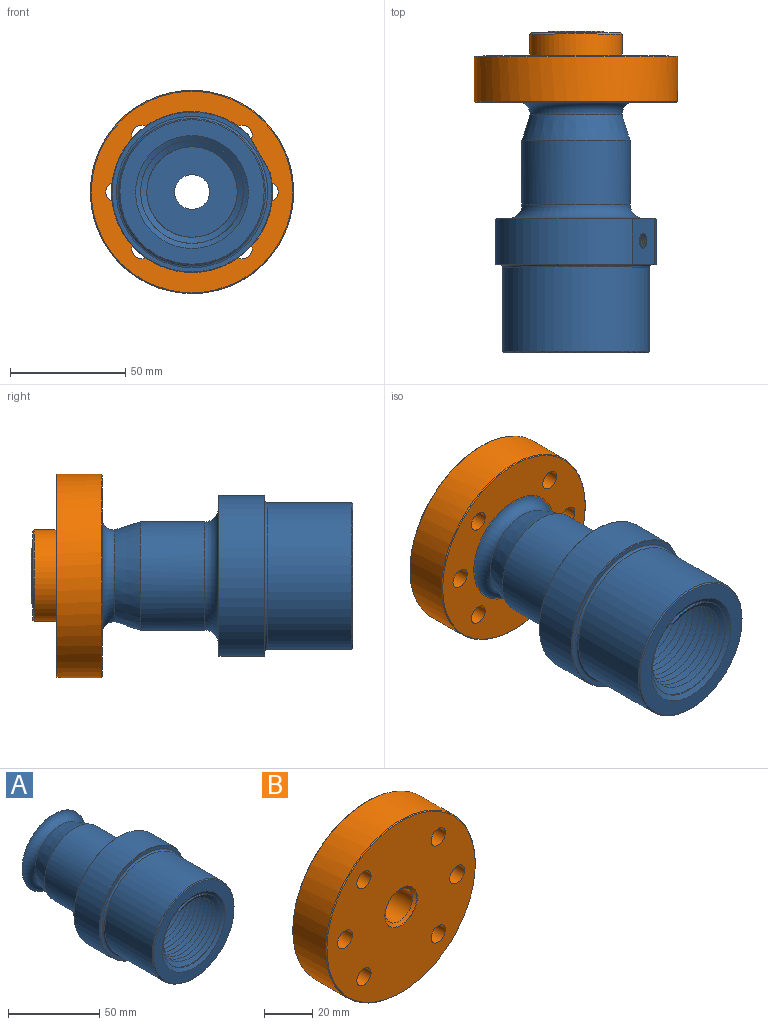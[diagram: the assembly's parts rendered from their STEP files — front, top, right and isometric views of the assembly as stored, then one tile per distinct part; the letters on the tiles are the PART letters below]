
ASSEMBLY  parts=2 mates=1
PART A: 31 faces, bbox 72.5x108.6x72.5 mm
  f0: plane 20.08x16.47mm, normal (0.87,0,0.5), area 349.2mm2, adj f1,f11,f13,f14,f15,f16,f28,f30
  f1: cylinder r=3.17mm len=10.87mm, axis (0.87,0,0.5), area 174.3mm2, adj f0,f17,f28,f30
  f2: cylinder r=22.23mm len=44.45mm, axis (0,1,0), area 277.8mm2, adj f22,f23,f24,f26,f27
  f3: plane 40.14x39.94mm, normal (0,-1,0), area 1077.6mm2, adj f12,f22,f26,f27
  f4: cone r=24.59mm half-angle=89.7deg, axis (0,1,0), area 1614.5mm2, adj f6,f9
  f5: torus R=29.42mm, axis (0,1,0), area 1464.9mm2, adj f8,f14
  f6: torus R=24.92mm, axis (0,1,0), area 1074.7mm2, adj f4,f7
  f7: cone r=19.93mm half-angle=17.6deg, axis (0,-1,0), area 1574.5mm2, adj f6,f8
  f8: cylinder r=23.43mm len=46.86mm, axis (0,1,0), area 4128.4mm2, adj f5,f7
  f9: cylinder r=9.53mm len=50.21mm, axis (0,-1,0), area 3004.8mm2, adj f4,f10
  f10: plane 19.05x19.05mm, normal (0,1,0), area 107.2mm2, adj f9,f12
  f11: cylinder r=34.87mm len=69.75mm, axis (0,1,0), area 3909.1mm2, adj f0,f15,f16
  f12: cylinder r=7.52mm len=20.07mm, axis (0,1,0), area 948.4mm2, adj f3,f10
  f13: plane 69.24x69.24mm, normal (0,-1,0), area 385.6mm2, adj f0,f15,f20
  f14: plane 69.24x69.24mm, normal (0,1,0), area 1058.3mm2, adj f0,f5,f16
  f15: cone r=34.62mm half-angle=45deg, axis (0,1,0), area 71.9mm2, adj f0,f11,f13
  f16: cone r=34.87mm half-angle=45deg, axis (0,-1,0), area 71.9mm2, adj f0,f11,f14
  f17: cone r=0mm half-angle=59deg, axis (0.87,0,0.5), area 36.9mm2, adj f1,f29
  f18: cylinder r=31.75mm len=63.5mm, axis (0,1,0), area 7301.7mm2, adj f20,f21
  f19: plane 62.48x62.48mm, normal (0,-1,0), area 1192.2mm2, adj f21,f23
  f20: torus R=32.74mm, axis (0,-1,0), area 313.9mm2, adj f13,f18
  f21: cone r=31.24mm half-angle=45deg, axis (0,1,0), area 142.2mm2, adj f18,f19
  f22: cone r=20.03mm half-angle=60deg, axis (0,-1,0), area 146.5mm2, adj f2,f3,f26,f27
  f23: cone r=22.23mm half-angle=60deg, axis (0,-1,0), area 372.2mm2, adj f2,f19,f25
  f24: plane 3.05x2.29mm, normal (-0.87,0,-0.5), area 4mm2, adj f2,f25,f26,f27
  f25: cylinder r=22.23mm len=34.08mm, axis (0,1,0), area 39.7mm2, adj f23,f24,f26
  f26: bspline ~51.33x44.45mm, area 4644.4mm2, adj f2,f3,f22,f24,f25,f27
  f27: bspline ~51.33x44.45mm, area 4461.1mm2, adj f2,f3,f22,f24,f26
  f28: bspline ~10.24x9.23mm, area 10.7mm2, adj f0,f1,f29,f30
  f29: plane 0.3x0.2mm, normal (0.87,0,0.5), area 0mm2, adj f17,f28,f30
  f30: bspline ~10.25x9.23mm, area 11.2mm2, adj f0,f1,f28,f29
PART B: 28 faces, bbox 88x30.9x88 mm
  f0: plane 87.22x87.11mm, normal (0,1,0), area 4232.4mm2, adj f2,f5,f6,f7,f8,f9,f10,f12
  f1: cylinder r=43.99mm len=87.99mm, axis (0,1,0), area 5325.4mm2, adj f2,f12,f14,f23,f26
  f2: cone r=43.99mm half-angle=45deg, axis (0,-1,0), area 144.9mm2, adj f0,f1,f12,f14
  f3: cylinder r=7.94mm len=23.79mm, axis (0,1,0), area 1186.3mm2, adj f20,f25
  f4: plane 6.35x0.17mm, normal (0,1,0), area 1.1mm2, adj f12,f13,f14,f27
  f5: cylinder r=4.18mm len=20.07mm, axis (0,1,0), area 527.5mm2, adj f0,f11
  f6: cylinder r=4.35mm len=20.07mm, axis (0,1,0), area 548.1mm2, adj f0,f11
  f7: cylinder r=4.18mm len=20.07mm, axis (0,1,0), area 527.5mm2, adj f0,f11
  f8: cylinder r=4.35mm len=20.07mm, axis (0,1,0), area 548.1mm2, adj f0,f11
  f9: cylinder r=4.18mm len=20.07mm, axis (0,1,0), area 527.5mm2, adj f0,f11
  f10: cylinder r=4.18mm len=20.07mm, axis (0,1,0), area 527.5mm2, adj f0,f11
  f11: plane 87.22x87.22mm, normal (0,-1,0), area 5351.5mm2, adj f5,f6,f7,f8,f9,f10,f23,f24
  f12: plane 25.93x12.07mm, normal (-1,0,0), area 70mm2, adj f0,f1,f2,f4,f13,f15,f16,f22
  f13: plane 10.03x6.35mm, normal (0,0,-1), area 63.7mm2, adj f4,f12,f14,f16
  f14: plane 25.93x12.07mm, normal (1,0,0), area 70mm2, adj f0,f1,f2,f4,f13,f15,f16,f22
  f15: cylinder r=19.98mm len=39.95mm, axis (0,-1,0), area 1134.8mm2, adj f0,f12,f14,f22
  f16: plane 38.94x38.68mm, normal (0,1,0), area 690.1mm2, adj f12,f13,f14,f18,f22
  f17: cylinder r=8.26mm len=16.51mm, axis (0,-1,0), area 289.2mm2, adj f19,f20
  f18: cylinder r=12.51mm len=25.02mm, axis (0,-1,0), area 20mm2, adj f16,f21
  f19: plane 24x24mm, normal (0,1,0), area 238.4mm2, adj f17,f21
  f20: cone r=7.94mm half-angle=50deg, axis (0,1,0), area 21.1mm2, adj f3,f17
  f21: cone r=12mm half-angle=45deg, axis (0,-1,0), area 55.3mm2, adj f18,f19
  f22: cone r=19.47mm half-angle=45deg, axis (0,-1,0), area 84.4mm2, adj f12,f14,f15,f16
  f23: cone r=43.61mm half-angle=45deg, axis (0,1,0), area 148.3mm2, adj f1,f11
  f24: cylinder r=9.53mm len=19.05mm, axis (0,-1,0), area 16.6mm2, adj f11,f25
  f25: cone r=0mm half-angle=59deg, axis (0,-1,0), area 101.6mm2, adj f3,f24
  f26: plane 25.88x6.35mm, normal (0,1,0), area 164.1mm2, adj f1,f12,f14,f27
  f27: plane 6.35x2.03mm, normal (0,0,-1), area 12.9mm2, adj f4,f12,f14,f26
PLACE A t=(-0.56,31.18,23.08)mm
PLACE B t=(-0.56,30.91,23.08)mm
MATE parallel A.f2 <-> B.f1  axis (0,1,0) through (-0.56,10.84,23.08)mm
